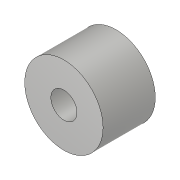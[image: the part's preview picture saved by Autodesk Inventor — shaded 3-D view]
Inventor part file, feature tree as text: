
AUTODESK INVENTOR PART (.ipt)
format: ipt  version: 2018.3 (Build 223284000, 284)  size: 83,456 bytes
history: native  units: in
note: dims shown in document units (in); Inventor stores cm internally (conversion verified against a paired STEP export)
features: extrude x1, sketch x1
ambient origin geometry x8: Origin, YZ Plane, XZ Plane, XY Plane, X Axis, Y Axis, Z Axis, Center Point
bodies: Solid1 (feature_tree)
feature tree (2):
  extrude  "Extrusion1"  Depth=0.25in
  sketch  "Sketch1"  dims[d0=0.125in d1=0.375in d2=0.25in d3=0.0in]
